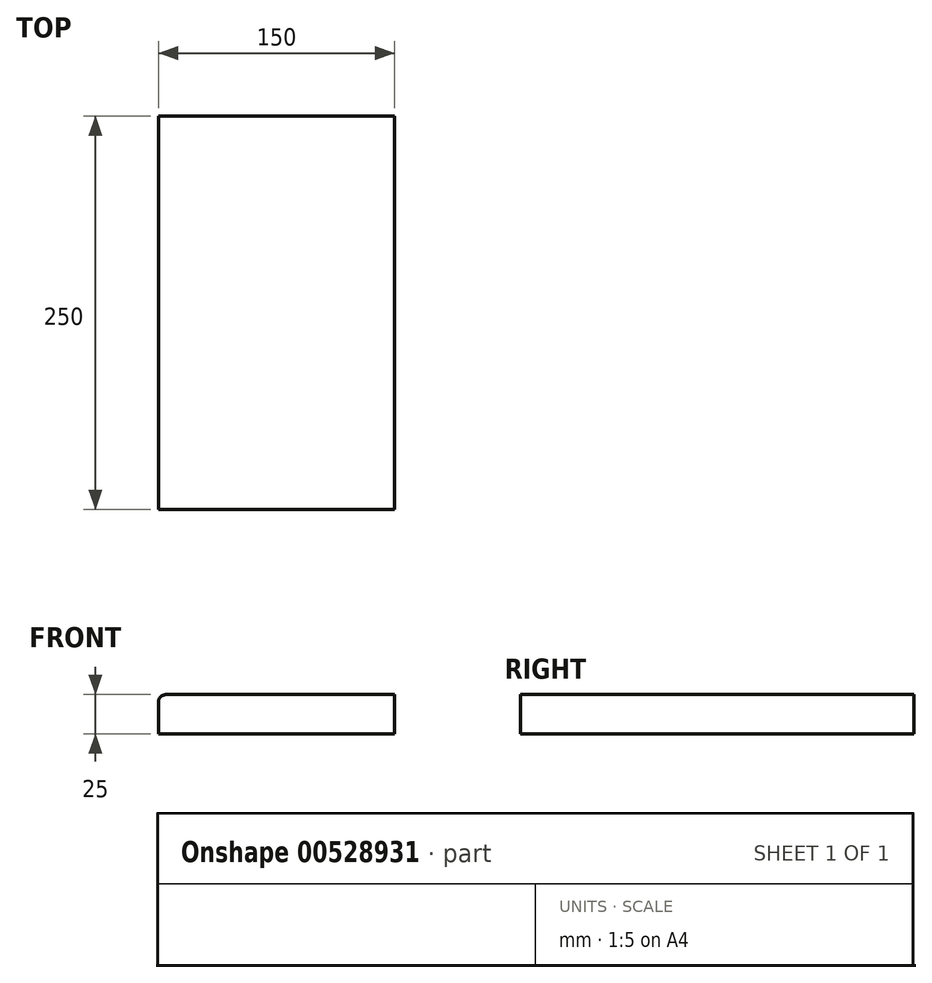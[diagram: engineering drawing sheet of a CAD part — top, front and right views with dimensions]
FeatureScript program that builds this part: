
annotation { "Feature Type Name" : "Feature", "Feature Type Description" : "" }
export const myFeature = defineFeature(function(context is Context, id is Id, definition is map)
    precondition{}
    {
        {
            var Q0;
            Q0=qCreatedBy(makeId("Top.planeOp"),FACE);
            var sketch = newSketch(context, id + "F0", { "sketchPlane" : qUnion([Q0])});
            skLineSegment(sketch, "E0.bottom", {"start": v(-75, 125) * mm, "end": v(75, 125) * mm});
            skLineSegment(sketch, "E0.top", {"start": v(-75, -125) * mm, "end": v(75, -125) * mm});
            skLineSegment(sketch, "E0.left", {"start": v(-75, 125) * mm, "end": v(-75, -125) * mm});
            skLineSegment(sketch, "E0.right", {"start": v(75, 125) * mm, "end": v(75, -125) * mm});
            skPoint(sketch, "E0.middle", {"position": v(0, 0) * mm});
            skSolve(sketch);
        }
        {
            var Q0;
            Q0 = qSketchRegion(id + "F0", true);
            extrude(context, id + "F1", {"entities" : qUnion([Q0]), "depth" : 25 * mm, "offsetDistance" : 25 * mm});
        }
        {
            var Q0;
            Q0=makeQuery(id+"F1.opExtrude","CAP_EDGE",EDGE,{"disambiguationData":[OSD([sQuery(id+"F0.wireOp",EDGE,"E0.left")])],"isStart":false});
            fillet(context, id + "F2", {"entities" : qUnion([Q0]), "radius" : 5 * mm, "tangentPropagation" : true, "allowEdgeOverflow" : false});
        }
    });
